# Revit family: P2RL-P.BIM
name_source: partatom
category: Fire Alarm Devices
units: mm (PartAtom-declared; Revit-internal decimal feet)

## family parameters
Cut with Voids When Loaded = No
Host = Face
Maintain Annotation Orientation = Yes
OmniClass Number = 23.85.30.21
OmniClass Title = Environmental Detection/Registration
Part Type = Normal
Room Calculation Point = No
Round Connector Dimension = Use Diameter
Shared = No

## types (2) — shared parameters
Assembly Code = D5030700
Default Elevation = 6' - 8"
Depth = 0' - 4 9/16"
Length = 0' - 6 9/16"
Main Electrical Connector = NAC
Manufacturer = System Sensor
URL = www.systemsensor.com
Width = 0' - 5"

## per-type parameters (varying)
| type | Backbox | Base Model | Description | Model |
| White-Compact | L-Series_Horn-Strobe_Wall-Mounted-Compact_Backbox : White Compact SMBB | L-Series_Horn-Strobe_Compact_Wall-Mounted : White_FIRE | Strobe Compact White | P2WL-P |
| Red_Compact | L-Series_Horn-Strobe_Wall-Mounted-Compact_Backbox : Red Compact SMBB | L-Series_Horn-Strobe_Compact_Wall-Mounted : Red_FIRE | Strobe Compact Red | P2RL-P |

## geometry (parser evidence)
native form markers: Blend x13, Sweep x8
no freeform markers — native parametric forms only
